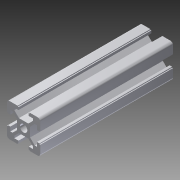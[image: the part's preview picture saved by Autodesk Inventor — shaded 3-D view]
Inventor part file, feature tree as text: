
AUTODESK INVENTOR PART (.ipt)
format: ipt  version: 2015 SP1 (Build 190203100, 203)  size: 157,184 bytes
history: native  units: mm
features: extrude x2, mirror x2, sketch x2, fillet x1
ambient origin geometry x8: Origin, YZ Plane, XZ Plane, XY Plane, X Axis, Y Axis, Z Axis, Center Point
bodies: Solid1 (feature_tree)
feature tree (7):
  extrude  "Extrusion1"  Depth=10.0mm
  fillet  "Fillet1"  Radius=10.0mm
  mirror  "Mirror1"
  mirror  "Mirror2"
  extrude  "Extrusion2"  Depth=6.1mm
  sketch  "Sketch1"  dims[d0=45.0deg d1=5.63mm d2=10.0mm]
  sketch  "Sketch2"  dims[d3=3.1mm d5=6.1mm d6=1.5mm d7=2.0mm d8=80.0mm d9=0.0mm d10=1.5mm d11=3.6mm d12=4.45mm d13=10.0mm d14=0.0mm]
